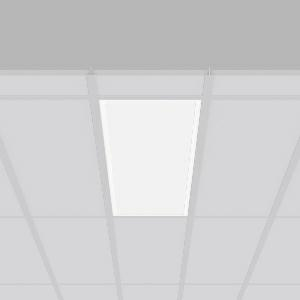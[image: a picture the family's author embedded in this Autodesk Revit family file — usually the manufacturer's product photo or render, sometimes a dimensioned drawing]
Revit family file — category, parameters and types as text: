
# Revit family: sidelite_eco_672372_002_1_07_4183
name_source: partatom
category: Lighting Fixtures
units: mm (PartAtom-declared; Revit-internal decimal feet)

## family parameters
Cut with Voids When Loaded = No
Host = Face
Light Source = No
Part Type = Normal
Room Calculation Point = No
Round Connector Dimension = Use Diameter
Shared = No

## types (1)
- SIDELITE ECO (1 x LED Modul 840, 3550 lm, 4000)
    Apparent Load = 29 VA
    CIE Flux Codes = 46 79 96 100 100
    Color Rendering = 80
    Color Temperature = 4000
    Default Elevation = 1800 mm
    Description = Series: SIDELITE ECO
Highly economical recessed luminaire with progressive LED technology. For escape route illumination. Frame made of aluminium, powder-coated. Diffuser: plastic, opal. Lightguide and diffuser made of non-yellowing plastic (PMMA). Lateral light emission (RZB SIDELITE technology) for homogeneous light distribution. External driver. Self-contained system with automatic self-test and feedback via DALI bus, only to RZB DALI monitoring system. External driver with simple plug-in locking system. Extended connection cable (1.90 m). 
Colour: white
Length: 1195 mm
Width: 295 mm
Cut-out length: 1170 mm
Cut-out width: 270 mm
Recess height: 160 mm
Luminaire: recess height: 40 mm
Weight: 4.42 kg
Operating mode: maintained power mode
Duration time: 8 h
Lamp: LED
Socket: without socket
Colour temperature: 4000K
Colour rendering index (CRI): 80
System power: 29 W
Rated luminous flux: 3550 lm
Luminous flux, emergency: 240 lm
System power, emergency: -
Control gear: Regulated power supply
Protection class: I
Type of protection: IP 40
    Height = 0 mm  [stored 0 ft]
    Lamp = 1 x LED Modul 840
    Lamp Light Flux = 3550 lm
    Lamp count = 1
    Length = 1195 mm
    Lifetime = 50000 h
    Luminous efficacy = 122 lm/W
    Manufacturer = RZB
    ModVariant = No
    Model = 672372.002.1.07
    Mounting Place = Ceiling
    Mounting Type = Recessed
    Number of Poles = 1
    OnlyDefault = Yes
    Power Factor = 1
    Product Name = SIDELITE ECO
    Product group = Recessed modular luminaires
    ProductGroupID = 406
    Protection Class = Protection class I
    Protection Degree = IP 40
    RLX_Detail_Level = 1
    RLX_Emergency_Light_Flux = 240 lm
    RLX_Emergency_Type = 3
    RLX_Emergency_Type_DB = Yes
    RlxData = <blob elided: 30673 chars, md5=108c391c>
    Socket = socket
    Standby Power = 0 W
    System Light Flux = 3550 lm
    System Power = 29 W
    Type Comments = Product without accessories
    Type Image = 312365.002.jpg
    URL = http://relux.com
    VarID = ---
    Voltage = 230 V
    Voltage Range = 220-240 V
    Weight = 0.00 kg
    Width = 295 mm

note: [stored X ft] marks values corroborated as IEEE doubles in the binary element streams (Revit-internal decimal feet)

## geometry (parser evidence)
native form markers: Blend x4, Sweep x12
no freeform markers — native parametric forms only
